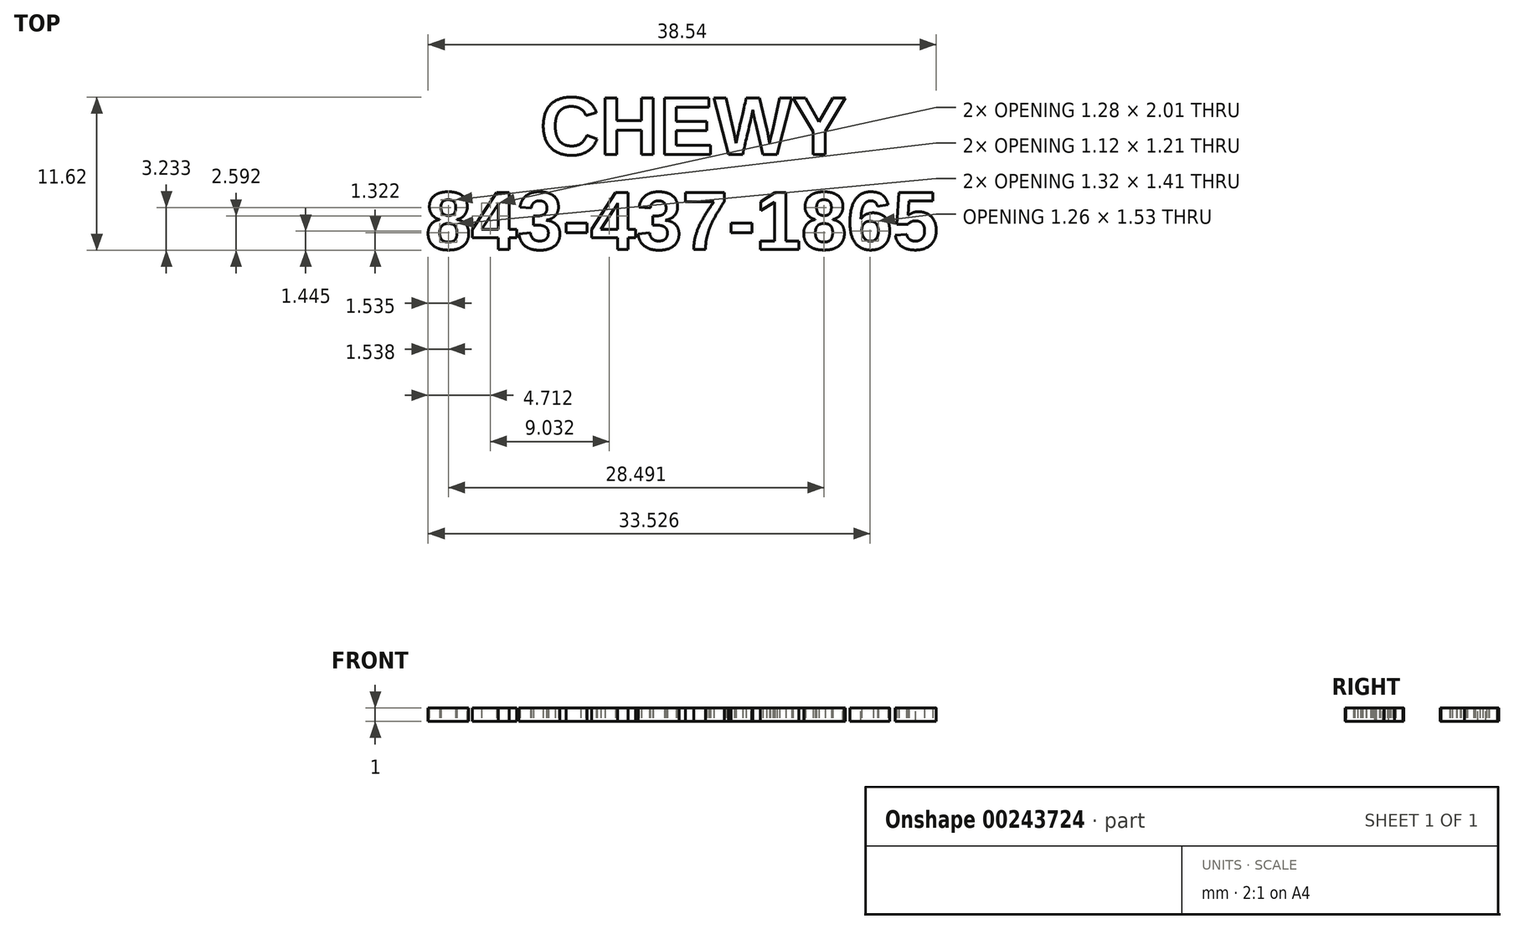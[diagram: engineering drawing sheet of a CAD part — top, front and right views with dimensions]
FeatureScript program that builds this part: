
annotation { "Feature Type Name" : "Feature", "Feature Type Description" : "" }
export const myFeature = defineFeature(function(context is Context, id is Id, definition is map)
    precondition{}
    {
        {
            var Q0;
            Q0=qCreatedBy(makeId("Top.planeOp"),FACE);
            var sketch = newSketch(context, id + "F0", { "sketchPlane" : qUnion([Q0])});
            skLineSegment(sketch, "E0.bottom", {"start": v(-25, 20) * mm, "end": v(25, 20) * mm});
            skLineSegment(sketch, "E0.top", {"start": v(-25, -20) * mm, "end": v(25, -20) * mm});
            skLineSegment(sketch, "E0.left", {"start": v(-25, 20) * mm, "end": v(-25, -20) * mm});
            skLineSegment(sketch, "E0.right", {"start": v(25, 20) * mm, "end": v(25, -20) * mm});
            skPoint(sketch, "E0.middle", {"position": v(0, 0) * mm});
            skSolve(sketch);
        }
        {
            var Q0;
            Q0=makeQuery(id+"FTcLUnwJZLc6uFZ_0.opExtrude","SWEPT_FACE",FACE,{"disambiguationData":[OSD([sQuery(id+"F0.wireOp",EDGE,"E0.left")])]});
            var sketch = newSketch(context, id + "F1", { "sketchPlane" : qUnion([Q0])});
            skLineSegment(sketch, "E1.bottom", {"start": v(-10, 5) * mm, "end": v(10, 5) * mm});
            skLineSegment(sketch, "E1.top", {"start": v(-10, 10) * mm, "end": v(10, 10) * mm});
            skLineSegment(sketch, "E1.left", {"start": v(-10, 5) * mm, "end": v(-10, 10) * mm});
            skLineSegment(sketch, "E1.right", {"start": v(10, 5) * mm, "end": v(10, 10) * mm});
            skPoint(sketch, "E1.middle", {"position": v(0, 7.5) * mm});
            skSolve(sketch);
        }
        {
            var Q0;
            Q0=makeQuery(id+"FTcLUnwJZLc6uFZ_0.opExtrude","SWEPT_FACE",FACE,{"disambiguationData":[OSD([sQuery(id+"F0.wireOp",EDGE,"E0.top")])]});
            var sketch = newSketch(context, id + "F2", { "sketchPlane" : qUnion([Q0])});
            skLineSegment(sketch, "E2.bottom", {"start": v(-15, 9) * mm, "end": v(15, 9) * mm});
            skLineSegment(sketch, "E2.top", {"start": v(-15, -9) * mm, "end": v(15, -9) * mm});
            skLineSegment(sketch, "E2.left", {"start": v(-15, 9) * mm, "end": v(-15, -9) * mm});
            skLineSegment(sketch, "E2.right", {"start": v(15, 9) * mm, "end": v(15, -9) * mm});
            skPoint(sketch, "E2.middle", {"position": v(0, 0) * mm});
            skSolve(sketch);
        }
        {
            var Q0;
            Q0=qCreatedBy(makeId("Top.planeOp"),FACE);
            cPlane(context, id + "F3", {"entities" : qUnion([Q0]), "cplaneType" : CPlaneType.OFFSET, "offset" : 14 * mm, "width" : 150 * mm, "height" : 150 * mm});
        }
        {
            var Q0;
            Q0=qCreatedBy(id+"F3.planeOp",FACE);
            var sketch = newSketch(context, id + "F4", { "sketchPlane" : qUnion([Q0])});
            skText(sketch, "E3", { "text": "     CHEWY\n843-437-1865", "fontName": "Arimo-Bold.ttf"});
            const initialGuessF4  = {"E3": [-0.01968, 0.00235, 1, 0, 0.0045]};
            skSetInitialGuess(sketch, initialGuessF4);
            skSolve(sketch);
        }
        {
            var Q0;
            Q0=qSketchRegion(id+"F4",true);
            extrude(context, id + "F5", {"entities" : qUnion([Q0]), "depth" : 1 * mm});
        }
    });
